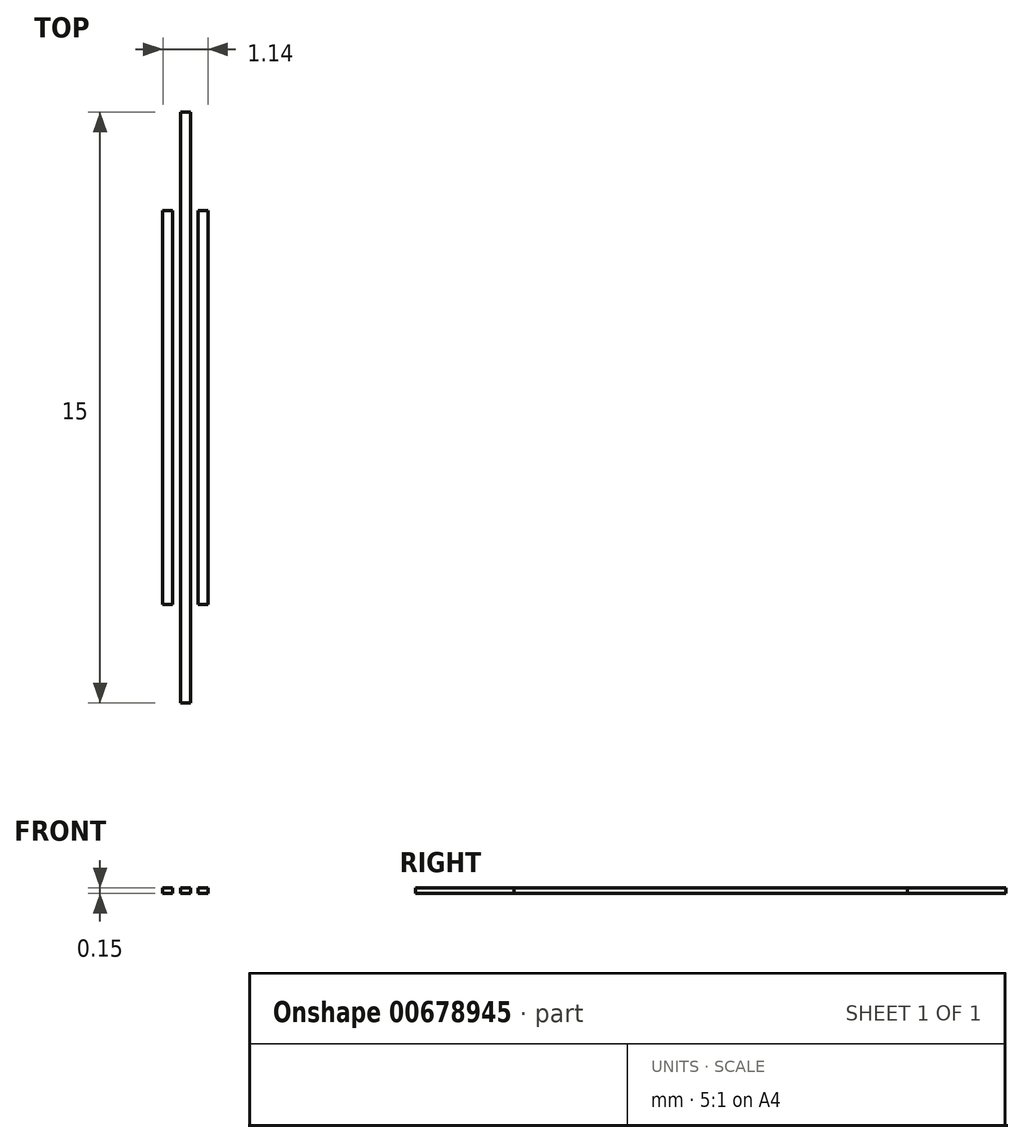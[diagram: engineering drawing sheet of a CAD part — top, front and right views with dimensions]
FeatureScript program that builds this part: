
annotation { "Feature Type Name" : "Feature", "Feature Type Description" : "" }
export const myFeature = defineFeature(function(context is Context, id is Id, definition is map)
    precondition{}
    {
        {
            var Q0;
            Q0=qCreatedBy(makeId("Top.planeOp"),FACE);
            var sketch = newSketch(context, id + "F0", { "sketchPlane" : qUnion([Q0])});
            skLineSegment(sketch, "E0.bottom", {"start": v(-0.33, 5) * mm, "end": v(-0.58, 5) * mm});
            skLineSegment(sketch, "E0.top", {"start": v(-0.33, -5) * mm, "end": v(-0.58, -5) * mm});
            skLineSegment(sketch, "E0.left", {"start": v(-0.33, 5) * mm, "end": v(-0.33, -5) * mm});
            skLineSegment(sketch, "E0.right", {"start": v(-0.58, 5) * mm, "end": v(-0.58, -5) * mm});
            skPoint(sketch, "E0.middle", {"position": v(-0.45, 0) * mm});
            skLineSegment(sketch, "E1.bottom", {"start": v(-0.13, 7.5) * mm, "end": v(0.12, 7.5) * mm});
            skLineSegment(sketch, "E1.top", {"start": v(-0.12, -7.5) * mm, "end": v(0.13, -7.5) * mm});
            skLineSegment(sketch, "E1.left", {"start": v(-0.13, 7.5) * mm, "end": v(-0.12, -7.5) * mm});
            skLineSegment(sketch, "E1.right", {"start": v(0.12, 7.5) * mm, "end": v(0.13, -7.5) * mm});
            skPoint(sketch, "E1.middle", {"position": v(0, 0) * mm});
            skLineSegment(sketch, "E2.bottom", {"start": v(0.33, 5) * mm, "end": v(0.58, 5) * mm});
            skLineSegment(sketch, "E2.top", {"start": v(0.32, -5) * mm, "end": v(0.57, -5) * mm});
            skLineSegment(sketch, "E2.left", {"start": v(0.33, 5) * mm, "end": v(0.32, -5) * mm});
            skLineSegment(sketch, "E2.right", {"start": v(0.58, 5) * mm, "end": v(0.58, -5) * mm});
            skPoint(sketch, "E2.middle", {"position": v(0.45, 0) * mm});
            skSolve(sketch);
        }
        {
            var Q0;
            Q0=makeQuery(id+"F0.imprint","IMPRINT",FACE,{"disambiguationData":[TD([[makeQuery(id+"F0.imprint","IMPRINT",EDGE,{"derivedFrom":sQuery(id+"F0.wireOp",EDGE,"E0.bottom")}),1.0]])]});
            var Q1;
            Q1=makeQuery(id+"F0.imprint","IMPRINT",FACE,{"disambiguationData":[TD([[makeQuery(id+"F0.imprint","IMPRINT",EDGE,{"derivedFrom":sQuery(id+"F0.wireOp",EDGE,"E1.bottom")}),-1.0]])]});
            var Q2;
            Q2=makeQuery(id+"F0.imprint","IMPRINT",FACE,{"disambiguationData":[TD([[makeQuery(id+"F0.imprint","IMPRINT",EDGE,{"derivedFrom":sQuery(id+"F0.wireOp",EDGE,"E2.bottom")}),-1.0]])]});
            extrude(context, id + "F1", {"entities" : qUnion([Q0, Q1, Q2]), "depth" : .15 * mm, "offsetDistance" : 25 * mm});
        }
    });
